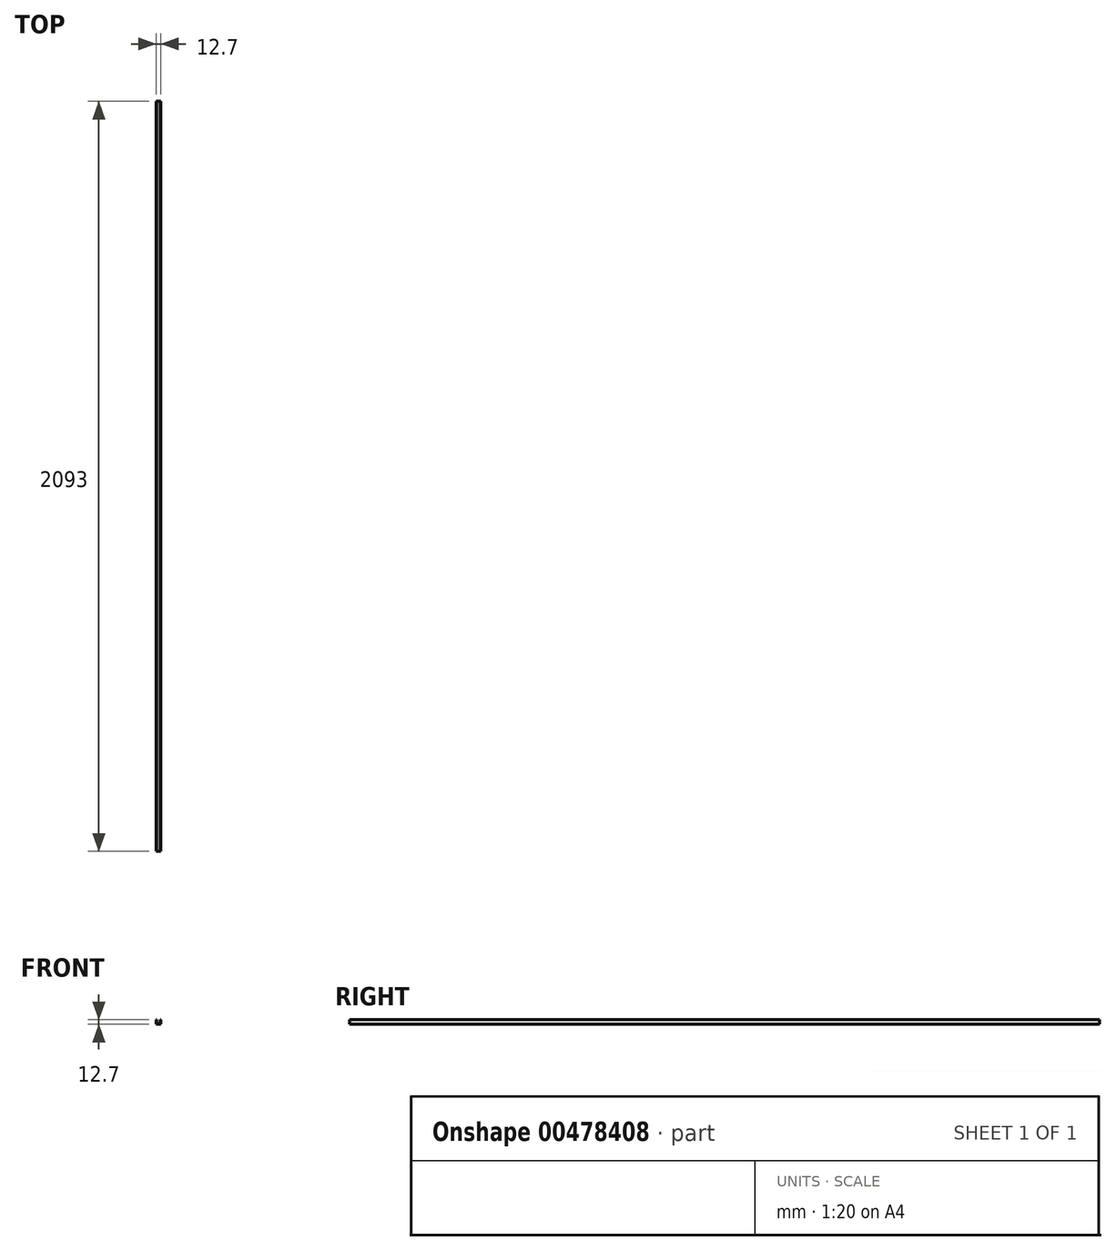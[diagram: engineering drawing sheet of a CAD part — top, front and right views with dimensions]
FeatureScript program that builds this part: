
annotation { "Feature Type Name" : "Feature", "Feature Type Description" : "" }
export const myFeature = defineFeature(function(context is Context, id is Id, definition is map)
    precondition{}
    {
        {
            var Q0;
            Q0=qCreatedBy(makeId("Front.planeOp"),FACE);
            var sketch = newSketch(context, id + "F0", { "sketchPlane" : qUnion([Q0])});
            skLineSegment(sketch, "E0", {"start": v(-35.59, 18.56) * mm, "end": v(-33.99, 18.56) * mm});
            skLineSegment(sketch, "E1", {"start": v(-35.59, 18.56) * mm, "end": v(-35.59, 5.86) * mm});
            skLineSegment(sketch, "E2", {"start": v(-35.59, 5.86) * mm, "end": v(-22.89, 5.86) * mm});
            skLineSegment(sketch, "E3", {"start": v(-22.89, 5.86) * mm, "end": v(-22.89, 18.56) * mm});
            skLineSegment(sketch, "E4", {"start": v(-33.99, 18.56) * mm, "end": v(-33.99, 5.86) * mm});
            skLineSegment(sketch, "E5.0", {"start": v(-35.59, 7.56) * mm, "end": v(-22.89, 7.56) * mm});
            skLineSegment(sketch, "E6.0", {"start": v(-24.59, 5.86) * mm, "end": v(-24.59, 18.56) * mm});
            skLineSegment(sketch, "E7", {"start": v(-24.59, 18.56) * mm, "end": v(-22.89, 18.56) * mm});
            skSolve(sketch);
        }
        {
            var Q0;
            {var subQ0=sQuery(id+"F0.wireOp",EDGE,"E0");Q0=makeQuery(id+"F0.imprint","IMPRINT",FACE,{"disambiguationData":[TD([[makeQuery(id+"F0.imprint","IMPRINT",EDGE,{"derivedFrom":subQ0}),-1.0]])]});}
            var Q1;
            {var subQ0=sQuery(id+"F0.wireOp",EDGE,"E2");var subQ1=sQuery(id+"F0.wireOp",EDGE,"E1");var subQ2=makeQuery(id+"F0.imprint","INTERSECT",VERTEX,{"derivedFrom":[subQ1,subQ0]});Q1=makeQuery(id+"F0.imprint","IMPRINT",FACE,{"disambiguationData":[TD([[makeQuery(id+"F0.imprint","IMPRINT",EDGE,{"disambiguationData":[TD([[subQ2,1.0]])],"derivedFrom":subQ1}),1.0]])]});}
            var Q2;
            {var subQ0=sQuery(id+"F0.wireOp",EDGE,"E4");var subQ1=sQuery(id+"F0.wireOp",EDGE,"E2");var subQ2=makeQuery(id+"F0.imprint","INTERSECT",VERTEX,{"derivedFrom":[subQ1,subQ0]});Q2=makeQuery(id+"F0.imprint","IMPRINT",FACE,{"disambiguationData":[TD([[makeQuery(id+"F0.imprint","IMPRINT",EDGE,{"disambiguationData":[TD([[subQ2,-1.0]])],"derivedFrom":subQ1}),1.0]])]});}
            var Q3;
            {var subQ0=sQuery(id+"F0.wireOp",EDGE,"E3");var subQ1=sQuery(id+"F0.wireOp",EDGE,"E2");var subQ2=makeQuery(id+"F0.imprint","INTERSECT",VERTEX,{"derivedFrom":[subQ1,subQ0]});Q3=makeQuery(id+"F0.imprint","IMPRINT",FACE,{"disambiguationData":[TD([[makeQuery(id+"F0.imprint","IMPRINT",EDGE,{"disambiguationData":[TD([[subQ2,1.0]])],"derivedFrom":subQ1}),1.0]])]});}
            var Q4;
            {var subQ0=sQuery(id+"F0.wireOp",EDGE,"E7");Q4=makeQuery(id+"F0.imprint","IMPRINT",FACE,{"disambiguationData":[TD([[makeQuery(id+"F0.imprint","IMPRINT",EDGE,{"derivedFrom":subQ0}),-1.0]])]});}
            extrude(context, id + "F1", {"entities" : qUnion([Q0, Q1, Q2, Q3, Q4]), "depth" : 2093 * mm});
        }
    });
